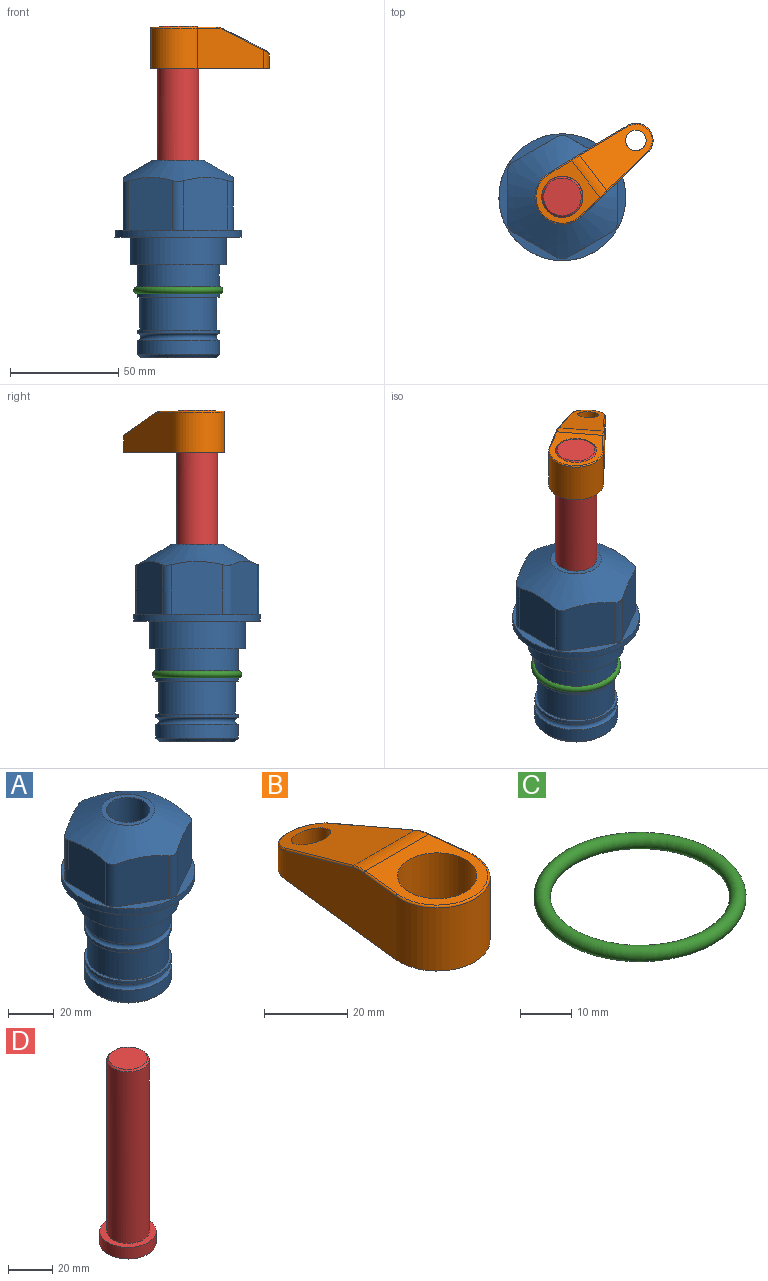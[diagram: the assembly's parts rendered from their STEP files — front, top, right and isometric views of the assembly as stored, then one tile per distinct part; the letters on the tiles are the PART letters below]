
ASSEMBLY  parts=4 mates=2
PART A: 36 faces, bbox 58.7x58.7x91.2 mm
  f0: cylinder r=17.78mm len=35.56mm, axis (0,0,1), area 1670.8mm2, adj f23,f24,f31
  f1: cylinder r=19.05mm len=38.1mm, axis (0,0,1), area 1191.9mm2, adj f26,f27,f30
  f2: plane 58.66x58.66mm, normal (0,0,-1), area 1150.6mm2, adj f3,f28
  f3: cylinder r=29.33mm len=58.66mm, axis (0,0,-1), area 585.1mm2, adj f2,f4
  f4: plane 58.66x58.66mm, normal (0,0,1), area 475.9mm2, adj f3,f5,f6,f7,f8,f9,f10,f11
  f5: plane 24.5x20.32mm, normal (-0.5,0.87,0), area 562.8mm2, adj f4,f15,f16,f17
  f6: plane 24.5x20.32mm, normal (0.5,0.87,0), area 562.8mm2, adj f4,f14,f15,f17
  f7: plane 24.5x23.48mm, normal (1,0,0), area 562.8mm2, adj f4,f13,f14,f17
  f8: plane 24.5x20.32mm, normal (0.5,-0.87,0), area 562.8mm2, adj f4,f12,f13,f17
  f9: plane 24.5x20.32mm, normal (-0.5,-0.87,0), area 562.8mm2, adj f4,f11,f12,f17
  f10: plane 24.5x23.48mm, normal (-1,0,0), area 562.8mm2, adj f4,f11,f16,f17
  f11: cylinder r=5.08mm len=23.01mm, axis (0,0,-1), area 121.2mm2, adj f4,f9,f10,f17
  f12: cylinder r=5.08mm len=23.01mm, axis (0,0,-1), area 121.2mm2, adj f4,f8,f9,f17
  f13: cylinder r=5.08mm len=23.01mm, axis (0,0,-1), area 121.2mm2, adj f4,f7,f8,f17
  f14: cylinder r=5.08mm len=23.01mm, axis (0,0,-1), area 121.2mm2, adj f4,f6,f7,f17
  f15: cylinder r=5.08mm len=23.01mm, axis (0,0,-1), area 121.2mm2, adj f4,f5,f6,f17
  f16: cylinder r=5.08mm len=23.01mm, axis (0,0,-1), area 121.2mm2, adj f4,f5,f10,f17
  f17: cone r=11.73mm half-angle=60deg, axis (0,0,-1), area 2071.8mm2, adj f5,f6,f7,f8,f9,f10,f11,f12
  f18: plane 23.46x23.46mm, normal (0,0,1), area 147.4mm2, adj f17,f35
  f19: plane 34.93x34.93mm, normal (0,0,-1), area 958mm2, adj f29
  f20: cylinder r=19.05mm len=38.1mm, axis (0,0,1), area 760.1mm2, adj f21,f29
  f21: torus R=19.05mm, axis (0,0,1), area 565.3mm2, adj f20,f22
  f22: cylinder r=19.05mm len=38.1mm, axis (0,0,1), area 190mm2, adj f21,f23
  f23: plane 38.1x38.1mm, normal (0,0,1), area 146.9mm2, adj f0,f22
  f24: plane 38.1x38.1mm, normal (0,0,-1), area 146.9mm2, adj f0,f25
  f25: cylinder r=19.05mm len=38.1mm, axis (0,0,1), area 190mm2, adj f24,f26
  f26: torus R=19.05mm, axis (0,0,1), area 565.3mm2, adj f1,f25
  f27: plane 44.45x44.45mm, normal (0,0,-1), area 411.7mm2, adj f1,f28
  f28: cylinder r=22.23mm len=44.45mm, axis (0,0,1), area 1773.5mm2, adj f2,f27
  f29: cone r=19.05mm half-angle=45deg, axis (0,0,1), area 257.5mm2, adj f19,f20
  f30: cylinder r=3.17mm len=6.75mm, axis (-1,0,0), area 128mm2, adj f1,f33
  f31: cylinder r=3.17mm len=6.35mm, axis (-1,0,0), area 102.5mm2, adj f0,f33
  f32: plane 25.4x25.4mm, normal (0,0,1), area 506.7mm2, adj f33
  f33: cylinder r=12.7mm len=66.42mm, axis (0,0,-1), area 5236.2mm2, adj f30,f31,f32,f34
  f34: cone r=9.53mm half-angle=30deg, axis (0,0,-1), area 443.4mm2, adj f33,f35
  f35: cylinder r=9.53mm len=19.05mm, axis (0,0,-1), area 849mm2, adj f18,f34
PART B: 44 faces, bbox 27.5x64.5x19.1 mm
  f0: plane 2.3x0.95mm, normal (0,0,-1), area 1mm2, adj f25,f30,f34
  f1: plane 63.5x25.4mm, normal (0,0,-1), area 561.7mm2, adj f2,f3,f4,f5,f6,f7,f19,f20
  f2: cylinder r=12.7mm len=25.4mm, axis (0,0,-1), area 792.2mm2, adj f1,f3,f5,f13
  f3: plane 42.33x18.54mm, normal (0.99,0.11,0), area 647mm2, adj f1,f2,f4,f11,f12,f14
  f4: cylinder r=7.94mm len=15.78mm, axis (0,0,-1), area 158.6mm2, adj f1,f3,f5,f16
  f5: plane 42.33x18.54mm, normal (-0.99,0.11,0), area 647mm2, adj f1,f2,f4,f15,f17,f18
  f6: cylinder r=9.53mm len=19.05mm, axis (0,0,-1), area 1140.1mm2, adj f1,f8
  f7: cylinder r=4.76mm len=10.98mm, axis (0,0,-1), area 276.1mm2, adj f1,f9
  f8: plane 25.83x24.38mm, normal (0,0,1), area 262.2mm2, adj f6,f10,f11,f13,f15
  f9: plane 32.49x20.55mm, normal (0,0.34,0.94), area 489.9mm2, adj f7,f10,f14,f16,f18
  f10: cylinder r=12.7mm len=21.49mm, axis (-1,0,0), area 93.2mm2, adj f8,f9,f12,f17
  f11: cylinder r=0.51mm len=12.34mm, axis (0.11,-0.99,0), area 9.9mm2, adj f3,f8,f12,f13
  f12: bspline ~7.62x1.64mm, area 3.5mm2, adj f3,f10,f11,f14
  f13: torus R=12.19mm, axis (0,0,1), area 33.6mm2, adj f2,f8,f11,f15
  f14: cylinder r=0.51mm len=26.01mm, axis (0.1,-0.93,0.34), area 21.6mm2, adj f3,f9,f12,f16
  f15: cylinder r=0.51mm len=12.34mm, axis (0.11,0.99,0), area 9.9mm2, adj f5,f8,f13,f17
  f16: bspline ~15.78x7.05mm, area 15.7mm2, adj f4,f9,f14,f18
  f17: bspline ~7.62x1.64mm, area 3.5mm2, adj f5,f10,f15,f18
  f18: cylinder r=0.51mm len=26.01mm, axis (0.1,0.93,-0.34), area 21.6mm2, adj f5,f9,f16,f17
  f19: plane 21.6x14.29mm, normal (-0.99,-0.11,0), area 242.6mm2, adj f1,f26,f28,f34,f36,f38
  f20: plane 21.6x14.29mm, normal (0.99,-0.11,0), area 242.6mm2, adj f1,f27,f29,f37,f39,f41
  f21: cylinder r=12.7mm len=14.29mm, axis (0,0,-1), area 173.2mm2, adj f1,f26,f27,f30,f31,f33
  f22: cylinder r=7.94mm len=7.63mm, axis (0,0,-1), area 53.8mm2, adj f1,f28,f29,f42
  f23: plane 2.3x0.95mm, normal (0,0,-1), area 1mm2, adj f25,f33,f37
  f24: plane 17.94x12.32mm, normal (0,-0.34,-0.94), area 191.2mm2, adj f25,f38,f41,f42
  f25: cylinder r=9.53mm len=12.93mm, axis (-1,0,0), area 37.5mm2, adj f0,f23,f24,f31,f36,f39
  f26: cylinder r=1.59mm len=14.29mm, axis (0,0,-1), area 49mm2, adj f1,f19,f21,f32
  f27: cylinder r=1.59mm len=14.29mm, axis (0,0,-1), area 49mm2, adj f1,f20,f21,f35
  f28: cylinder r=1.59mm len=7.28mm, axis (0,0,-1), area 22.1mm2, adj f1,f19,f22,f40
  f29: cylinder r=1.59mm len=7.28mm, axis (0,0,-1), area 22.1mm2, adj f1,f20,f22,f43
  f30: torus R=14.29mm, axis (0,0,1), area 5.8mm2, adj f0,f21,f31,f32
  f31: bspline ~11.06x2.73mm, area 20.8mm2, adj f21,f25,f30,f33
  f32: sphere r=1.59mm, area 5.4mm2, adj f26,f30,f34
  f33: torus R=14.29mm, axis (0,0,1), area 5.8mm2, adj f21,f23,f31,f35
  f34: cylinder r=1.59mm len=1.68mm, axis (-0.11,0.99,0), area 2.4mm2, adj f0,f19,f32,f36
  f35: sphere r=1.59mm, area 5.4mm2, adj f27,f33,f37
  f36: bspline ~5.82x2.33mm, area 7.7mm2, adj f19,f25,f34,f38
  f37: cylinder r=1.59mm len=1.68mm, axis (0.11,0.99,0), area 2.4mm2, adj f20,f23,f35,f39
  f38: cylinder r=1.59mm len=18.33mm, axis (0.1,-0.93,0.34), area 46.7mm2, adj f19,f24,f36,f40
  f39: bspline ~5.82x2.33mm, area 7.7mm2, adj f20,f25,f37,f41
  f40: sphere r=1.59mm, area 3.6mm2, adj f28,f38,f42
  f41: cylinder r=1.59mm len=18.33mm, axis (0.1,0.93,-0.34), area 46.7mm2, adj f20,f24,f39,f43
  f42: bspline ~8.31x1.84mm, area 15.3mm2, adj f22,f24,f40,f43
  f43: sphere r=1.59mm, area 3.6mm2, adj f29,f41,f42
PART C: 1 faces, bbox 44.7x44.7x3.2 mm
  f0: torus R=19.05mm, axis (0,0,1), area 1193.9mm2
PART D: 6 faces, bbox 25.4x25.4x101.6 mm
  f0: plane 17.46x17.46mm, normal (0,0,1), area 239.5mm2, adj f5
  f1: plane 25.4x25.4mm, normal (0,0,-1), area 506.7mm2, adj f2
  f2: cylinder r=12.7mm len=25.4mm, axis (0,0,1), area 506.7mm2, adj f1,f3
  f3: plane 25.4x25.4mm, normal (0,0,1), area 221.7mm2, adj f2,f4
  f4: cylinder r=9.53mm len=94.46mm, axis (0,0,1), area 5653mm2, adj f3,f5
  f5: cone r=8.73mm half-angle=45deg, axis (0,0,-1), area 64.4mm2, adj f0,f4
PLACE A t=(-5.09,6.99,5.88)mm fixed
PLACE B rot(axis=(0,0,-1),52.5deg) t=(-5.09,6.99,84)mm
PLACE C t=(-5.09,6.99,5.88)mm
PLACE D rot(axis=(0,0,-1),52.5deg) t=(-5.09,6.99,29.67)mm
MATE fastened B.f2 <-> D.f2  axis (0,0,1) through (-5.09,6.99,102.54)mm
MATE cylindrical D.f2 <-> A.f0  axis (0,0,1) through (-5.09,6.99,55.31)mm
